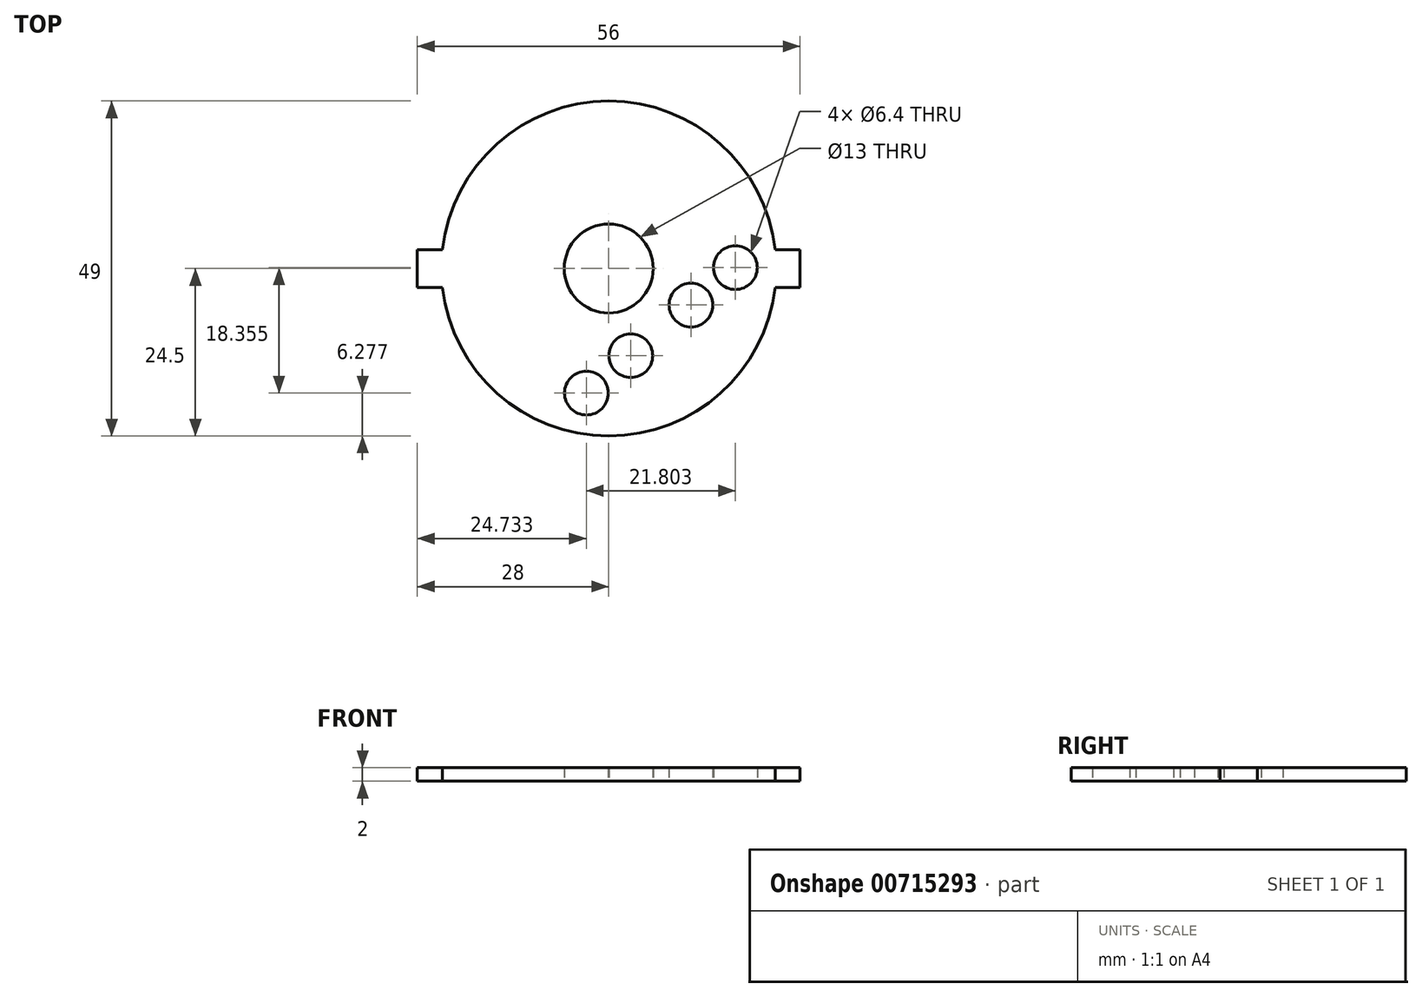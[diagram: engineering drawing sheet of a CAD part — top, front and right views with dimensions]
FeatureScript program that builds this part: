
annotation { "Feature Type Name" : "Feature", "Feature Type Description" : "" }
export const myFeature = defineFeature(function(context is Context, id is Id, definition is map)
    precondition{}
    {
        {
            var Q0;
            Q0=qCreatedBy(makeId("Top.planeOp"),FACE);
            var sketch = newSketch(context, id + "F0", { "sketchPlane" : qUnion([Q0])});
            skCircle(sketch, "E0", {"center": v(0, 0) * mm, "radius": 24.5 * mm});
            skLineSegment(sketch, "E1.bottom", {"start": v(-28, 2.75) * mm, "end": v(-21, 2.75) * mm});
            skLineSegment(sketch, "E1.top", {"start": v(-28, -2.75) * mm, "end": v(-21, -2.75) * mm});
            skLineSegment(sketch, "E1.left", {"start": v(-28, 2.75) * mm, "end": v(-28, -2.75) * mm});
            skLineSegment(sketch, "E1.right", {"start": v(-21, 2.75) * mm, "end": v(-21, -2.75) * mm});
            skPoint(sketch, "E1.middle", {"position": v(-24.5, 0) * mm});
            skLineSegment(sketch, "E2.MirrorCS", {"start": v(28, -2.75) * mm, "end": v(21, -2.75) * mm});
            skLineSegment(sketch, "E3.MirrorCS", {"start": v(28, 2.75) * mm, "end": v(28, -2.75) * mm});
            skLineSegment(sketch, "E4.MirrorCS", {"start": v(28, 2.75) * mm, "end": v(21, 2.75) * mm});
            skLineSegment(sketch, "E5.MirrorCS", {"start": v(21, 2.75) * mm, "end": v(21, -2.75) * mm});
            skCircle(sketch, "E6", {"center": v(0, 0) * mm, "radius": 6.5 * mm});
            skPoint(sketch, "E7.orphan", {"position": v(0, -12) * mm});
            skCircle(sketch, "E8", {"center": v(3.24, -12.75) * mm, "radius": 3.2 * mm});
            skCircle(sketch, "E9.MirrorC", {"center": v(12.03, -5.34) * mm, "radius": 3.2 * mm});
            skCircle(sketch, "E10.1.0.0", {"center": v(18.54, 0.13) * mm, "radius": 3.2 * mm});
            skCircle(sketch, "E11.1.0.0", {"center": v(-3.27, -18.22) * mm, "radius": 3.2 * mm});
            skLineSegment(sketch, "E12.0", {"start": v(3.24, -12.75) * mm, "end": v(12.03, -5.34) * mm, "construction": true});
            skLineSegment(sketch, "E12.1", {"start": v(3.24, -12.75) * mm, "end": v(3.24, -12.75) * mm});
            skSolve(sketch);
        }
        {
            var Q0;
            {var subQ4=sQuery(id+"F0.wireOp",EDGE,"E1.right");Q0=makeQuery(id+"F0.imprint","IMPRINT",FACE,{"disambiguationData":[TD([[makeQuery(id+"F0.imprint","IMPRINT",EDGE,{"derivedFrom":subQ4}),1.0]])]});}
            var Q1;
            {var subQ1=sQuery(id+"F0.wireOp",EDGE,"LHFyxg6Q-hmOt-jf90-2FeN-QkjvNVWxY9QZ");var subQ5=sQuery(id+"F0.wireOp",EDGE,"E0");var subQ6=makeQuery(id+"F0.imprint","INTERSECT",VERTEX,{"disambiguationData":[OD(0.0)],"derivedFrom":[subQ5,subQ1]});Q1=makeQuery(id+"F0.imprint","IMPRINT",FACE,{"disambiguationData":[TD([[makeQuery(id+"F0.imprint","IMPRINT",EDGE,{"disambiguationData":[TD([[subQ6,1.0]])],"derivedFrom":subQ5}),1.0]])]});}
            var Q2;
            {var subQ5=sQuery(id+"F0.wireOp",EDGE,"E1.right");Q2=makeQuery(id+"F0.imprint","IMPRINT",FACE,{"disambiguationData":[TD([[makeQuery(id+"F0.imprint","IMPRINT",EDGE,{"derivedFrom":subQ5}),-1.0]])]});}
            var Q3;
            {var subQ5=sQuery(id+"F0.wireOp",EDGE,"E1.left");Q3=makeQuery(id+"F0.imprint","IMPRINT",FACE,{"disambiguationData":[TD([[makeQuery(id+"F0.imprint","IMPRINT",EDGE,{"derivedFrom":subQ5}),1.0]])]});}
            var Q4;
            {var subQ5=sQuery(id+"F0.wireOp",EDGE,"E5.MirrorCS");Q4=makeQuery(id+"F0.imprint","IMPRINT",FACE,{"disambiguationData":[TD([[makeQuery(id+"F0.imprint","IMPRINT",EDGE,{"derivedFrom":subQ5}),1.0]])]});}
            var Q5;
            {var subQ5=sQuery(id+"F0.wireOp",EDGE,"E3.MirrorCS");Q5=makeQuery(id+"F0.imprint","IMPRINT",FACE,{"disambiguationData":[TD([[makeQuery(id+"F0.imprint","IMPRINT",EDGE,{"derivedFrom":subQ5}),-1.0]])]});}
            extrude(context, id + "F1", {"entities" : qUnion([Q0, Q1, Q2, Q3, Q4, Q5]), "depth" : 2 * mm, "offsetDistance" : 25 * mm});
        }
    });
